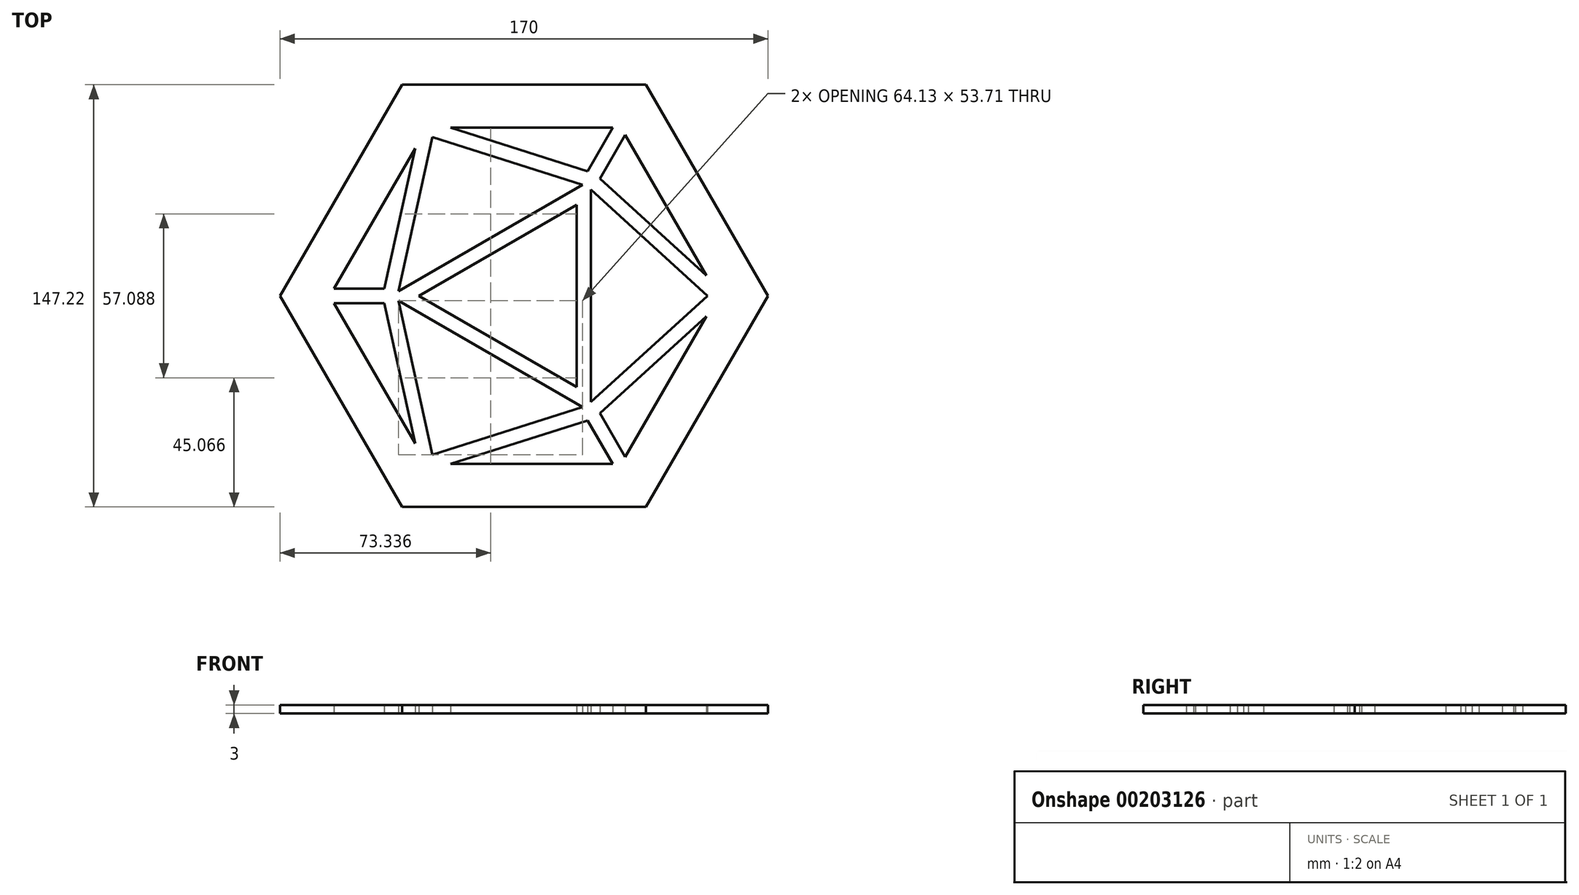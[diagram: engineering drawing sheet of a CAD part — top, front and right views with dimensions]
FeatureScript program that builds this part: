
annotation { "Feature Type Name" : "Feature", "Feature Type Description" : "" }
export const myFeature = defineFeature(function(context is Context, id is Id, definition is map)
    precondition{}
    {
        {
            var Q0;
            Q0=qCreatedBy(makeId("Top.planeOp"),FACE);
            var sketch = newSketch(context, id + "F0", { "sketchPlane" : qUnion([Q0])});
            skCircle(sketch, "E0.cCircle", {"center": v(0, 0) * mm, "radius": 73.61 * mm, "construction": true});
            skLineSegment(sketch, "E0.0", {"start": v(42.5, 73.61) * mm, "end": v(85, 0) * mm});
            skLineSegment(sketch, "E0.1", {"start": v(85, 0) * mm, "end": v(42.5, -73.61) * mm});
            skLineSegment(sketch, "E0.2", {"start": v(42.5, -73.61) * mm, "end": v(-42.5, -73.61) * mm});
            skLineSegment(sketch, "E0.3", {"start": v(-42.5, -73.61) * mm, "end": v(-85, 0) * mm});
            skLineSegment(sketch, "E0.4", {"start": v(-85, 0) * mm, "end": v(-42.5, 73.61) * mm});
            skLineSegment(sketch, "E0.5", {"start": v(-42.5, 73.61) * mm, "end": v(42.5, 73.61) * mm});
            skPoint(sketch, "E0.0.midPoint", {"position": v(63.75, 36.8) * mm});
            skCircle(sketch, "E1.cCircle", {"center": v(0, 0) * mm, "radius": 58.61 * mm, "construction": true});
            skLineSegment(sketch, "E1.0", {"start": v(33.84, 58.61) * mm, "end": v(67.68, 0) * mm});
            skLineSegment(sketch, "E1.1", {"start": v(67.68, 0) * mm, "end": v(33.84, -58.61) * mm});
            skLineSegment(sketch, "E1.2", {"start": v(-33.84, -58.61) * mm, "end": v(33.84, -58.61) * mm});
            skLineSegment(sketch, "E1.3", {"start": v(-33.84, -58.61) * mm, "end": v(-67.68, 0) * mm});
            skLineSegment(sketch, "E1.4", {"start": v(-67.68, 0) * mm, "end": v(-33.84, 58.61) * mm});
            skLineSegment(sketch, "E1.5", {"start": v(33.84, 58.61) * mm, "end": v(-33.84, 58.61) * mm});
            skPoint(sketch, "E1.0.midPoint", {"position": v(50.76, 29.3) * mm});
            skSolve(sketch);
        }
        {
            var Q0;
            Q0 = qSketchRegion(id + "F0", true);
            extrude(context, id + "F1", {"entities" : qUnion([Q0]), "depth" : 3 * mm});
        }
        {
            var Q0;
            Q0=qCreatedBy(makeId("Top.planeOp"),FACE);
            var sketch = newSketch(context, id + "F2", { "sketchPlane" : qUnion([Q0])});
            skCircle(sketch, "E2.cCircle", {"center": v(0, 0) * mm, "radius": 23.33 * mm, "construction": true});
            skLineSegment(sketch, "E2.0", {"start": v(20.4, -38.72) * mm, "end": v(-43.73, -1.7) * mm});
            skLineSegment(sketch, "E2.1", {"start": v(-43.73, 1.7) * mm, "end": v(20.4, 38.72) * mm});
            skLineSegment(sketch, "E2.2", {"start": v(23.33, 37.02) * mm, "end": v(23.33, -37.02) * mm});
            skPoint(sketch, "E2.0.midPoint", {"position": v(-11.66, -20.2) * mm});
            skCircle(sketch, "E3.cCircle", {"center": v(0, 0) * mm, "radius": 18.33 * mm, "construction": true});
            skLineSegment(sketch, "E3.0", {"start": v(18.33, 31.75) * mm, "end": v(18.33, -31.75) * mm});
            skLineSegment(sketch, "E3.1", {"start": v(18.33, -31.75) * mm, "end": v(-36.66, 0) * mm});
            skLineSegment(sketch, "E3.2", {"start": v(-36.66, 0) * mm, "end": v(18.33, 31.75) * mm});
            skPoint(sketch, "E3.0.midPoint", {"position": v(18.33, 0) * mm});
            skLineSegment(sketch, "E4", {"start": v(33.84, 58.61) * mm, "end": v(23.33, 40.4) * mm, "construction": true});
            skLineSegment(sketch, "E5", {"start": v(23.33, 40.4) * mm, "end": v(67.68, 0) * mm, "construction": true});
            skLineSegment(sketch, "E6", {"start": v(23.33, 40.4) * mm, "end": v(-33.84, 58.61) * mm, "construction": true});
            skLineSegment(sketch, "E7", {"start": v(22.17, 43.4) * mm, "end": v(-25.6, 58.61) * mm});
            skLineSegment(sketch, "E8.MirrorCS", {"start": v(23.33, 37.02) * mm, "end": v(63.97, 0) * mm});
            skLineSegment(sketch, "E9.MirrorCS", {"start": v(26.5, 40.9) * mm, "end": v(63.56, 7.13) * mm});
            skLineSegment(sketch, "E10", {"start": v(22.17, 43.4) * mm, "end": v(30.95, 58.61) * mm});
            skLineSegment(sketch, "E11", {"start": v(26.5, 40.9) * mm, "end": v(35.28, 56.11) * mm});
            skLineSegment(sketch, "E12", {"start": v(-33.84, 58.61) * mm, "end": v(-46.66, 0) * mm, "construction": true});
            skLineSegment(sketch, "E13", {"start": v(-46.66, 0) * mm, "end": v(-67.68, 0) * mm, "construction": true});
            skLineSegment(sketch, "E14", {"start": v(-46.66, 0) * mm, "end": v(-33.84, -58.61) * mm, "construction": true});
            skLineSegment(sketch, "E15", {"start": v(23.33, -40.4) * mm, "end": v(-33.84, -58.61) * mm, "construction": true});
            skLineSegment(sketch, "E16", {"start": v(23.33, -40.4) * mm, "end": v(33.84, -58.61) * mm, "construction": true});
            skLineSegment(sketch, "E17", {"start": v(67.68, 0) * mm, "end": v(23.33, -40.4) * mm, "construction": true});
            skLineSegment(sketch, "E18", {"start": v(63.97, 0) * mm, "end": v(23.33, -37.02) * mm});
            skLineSegment(sketch, "E19", {"start": v(63.56, -7.13) * mm, "end": v(26.5, -40.9) * mm});
            skLineSegment(sketch, "E20", {"start": v(35.28, -56.11) * mm, "end": v(26.5, -40.9) * mm});
            skLineSegment(sketch, "E21", {"start": v(-25.6, -58.61) * mm, "end": v(22.17, -43.4) * mm});
            skLineSegment(sketch, "E22", {"start": v(30.95, -58.61) * mm, "end": v(22.17, -43.4) * mm});
            skLineSegment(sketch, "E23", {"start": v(20.4, -38.72) * mm, "end": v(-31.98, -55.4) * mm});
            skLineSegment(sketch, "E24", {"start": v(-31.98, -55.4) * mm, "end": v(-43.73, -1.7) * mm});
            skLineSegment(sketch, "E25", {"start": v(-66.24, -2.5) * mm, "end": v(-48.67, -2.5) * mm});
            skLineSegment(sketch, "E26", {"start": v(-48.67, -2.5) * mm, "end": v(-37.96, -51.48) * mm});
            skLineSegment(sketch, "E27", {"start": v(-66.24, 2.5) * mm, "end": v(-48.67, 2.5) * mm});
            skLineSegment(sketch, "E28", {"start": v(-48.67, 2.5) * mm, "end": v(-37.96, 51.48) * mm});
            skLineSegment(sketch, "E29", {"start": v(20.4, 38.72) * mm, "end": v(-31.98, 55.4) * mm});
            skLineSegment(sketch, "E30", {"start": v(-43.73, 1.7) * mm, "end": v(-31.98, 55.4) * mm});
            skLineSegment(sketch, "E31", {"start": v(63.56, 7.13) * mm, "end": v(71.4, 0) * mm});
            skLineSegment(sketch, "E32", {"start": v(63.56, -7.13) * mm, "end": v(71.4, 0) * mm});
            skLineSegment(sketch, "E33", {"start": v(30.95, 58.61) * mm, "end": v(32.12, 61.42) * mm});
            skLineSegment(sketch, "E34", {"start": v(32.12, 61.42) * mm, "end": v(37.07, 58.61) * mm});
            skLineSegment(sketch, "E35", {"start": v(37.07, 58.61) * mm, "end": v(35.28, 56.11) * mm});
            skLineSegment(sketch, "E36", {"start": v(-37.96, 51.48) * mm, "end": v(-36.99, 64.07) * mm});
            skLineSegment(sketch, "E37", {"start": v(-25.6, 58.61) * mm, "end": v(-36.99, 64.07) * mm});
            skLineSegment(sketch, "E38", {"start": v(-66.24, 2.5) * mm, "end": v(-72.46, 1.44) * mm});
            skLineSegment(sketch, "E39", {"start": v(-72.46, 1.44) * mm, "end": v(-66.24, -2.5) * mm});
            skLineSegment(sketch, "E40", {"start": v(-37.96, -51.48) * mm, "end": v(-37.86, -64.18) * mm});
            skLineSegment(sketch, "E41", {"start": v(-25.6, -58.61) * mm, "end": v(-37.86, -64.18) * mm});
            skLineSegment(sketch, "E42", {"start": v(30.95, -58.61) * mm, "end": v(34.22, -60.35) * mm});
            skLineSegment(sketch, "E43", {"start": v(34.22, -60.35) * mm, "end": v(35.28, -56.11) * mm});
            skSolve(sketch);
        }
        {
            var Q0;
            Q0 = qSketchRegion(id + "F2", true);
            extrude(context, id + "F3", {"entities" : qUnion([Q0]), "operationType" : NewBodyOperationType.ADD, "depth" : 3 * mm});
        }
    });
